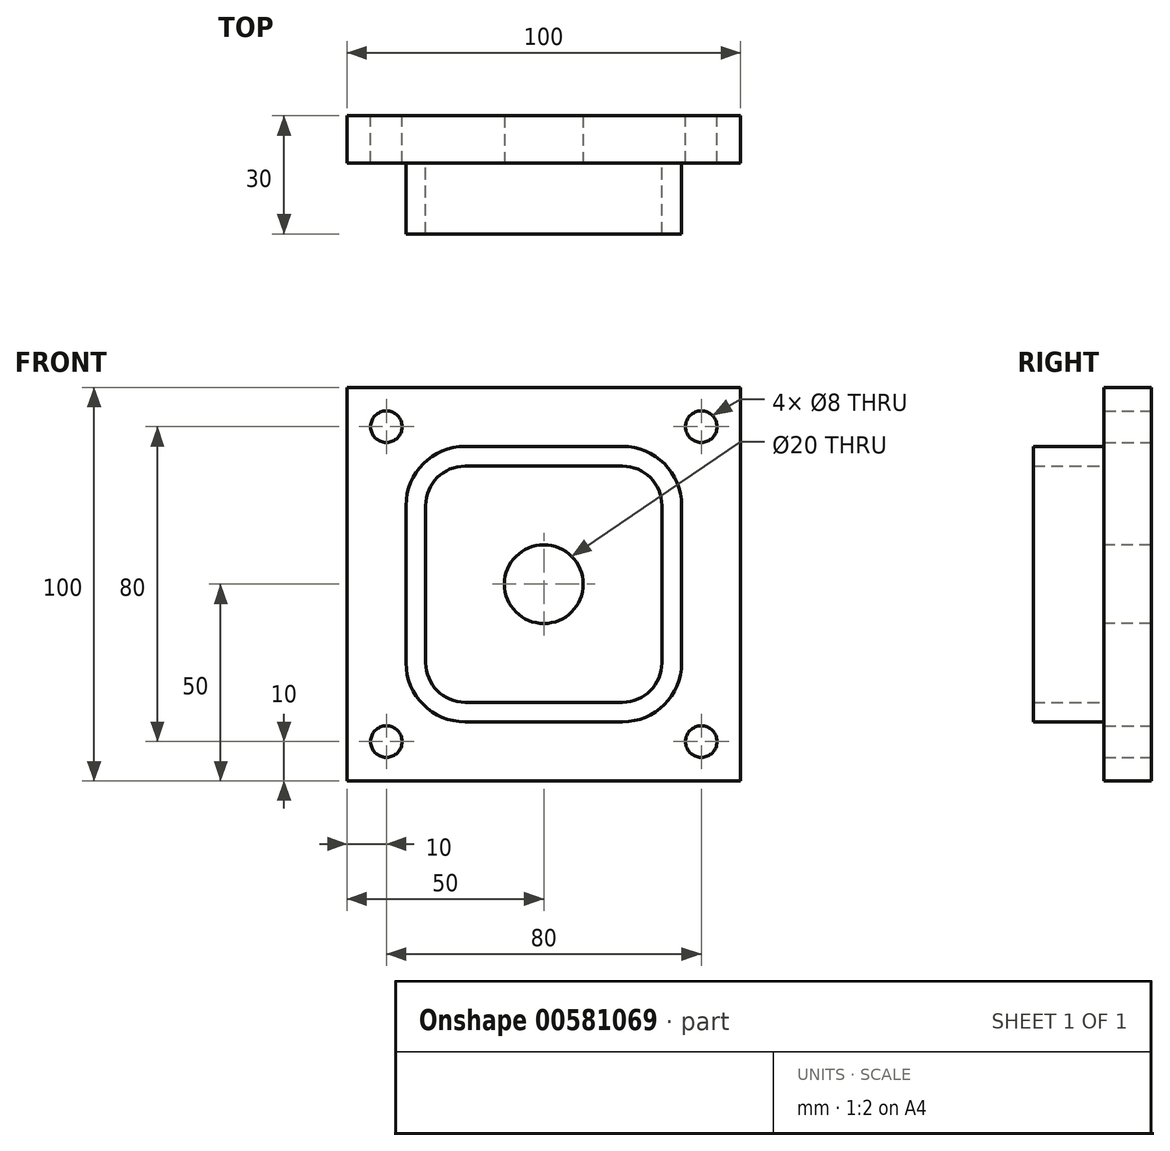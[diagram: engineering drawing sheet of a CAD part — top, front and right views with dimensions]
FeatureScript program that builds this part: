
annotation { "Feature Type Name" : "Feature", "Feature Type Description" : "" }
export const myFeature = defineFeature(function(context is Context, id is Id, definition is map)
    precondition{}
    {
        {
            var Q0;
            Q0=qCreatedBy(makeId("Front.planeOp"),FACE);
            var sketch = newSketch(context, id + "F0", { "sketchPlane" : qUnion([Q0])});
            skLineSegment(sketch, "E0.bottom", {"start": v(50, -50) * mm, "end": v(-50, -50) * mm});
            skLineSegment(sketch, "E0.top", {"start": v(50, 50) * mm, "end": v(-50, 50) * mm});
            skLineSegment(sketch, "E0.left", {"start": v(50, -50) * mm, "end": v(50, 50) * mm});
            skLineSegment(sketch, "E0.right", {"start": v(-50, -50) * mm, "end": v(-50, 50) * mm});
            skPoint(sketch, "E0.middle", {"position": v(0, 0) * mm});
            skCircle(sketch, "E1", {"center": v(-40, 40) * mm, "radius": 4 * mm});
            skCircle(sketch, "E2", {"center": v(-40, -40) * mm, "radius": 4 * mm});
            skCircle(sketch, "E3", {"center": v(40, 40) * mm, "radius": 4 * mm});
            skCircle(sketch, "E4", {"center": v(40, -40) * mm, "radius": 4 * mm});
            skSolve(sketch);
        }
        {
            var Q0;
            Q0=makeQuery(id+"F0.imprint","IMPRINT",FACE,{"disambiguationData":[TD([[makeQuery(id+"F0.imprint","IMPRINT",EDGE,{"derivedFrom":sQuery(id+"F0.wireOp",EDGE,"E0.bottom")}),-1.0]])]});
            extrude(context, id + "F1", {"entities" : qUnion([Q0]), "depth" : 12 * mm, "offsetDistance" : 25 * mm});
        }
        {
            var Q0;
            Q0=makeQuery(id+"F1.opExtrude","CAP_FACE",FACE,{"disambiguationData":[OSD([sQuery(id+"F0.wireOp",EDGE,"E0.bottom"),sQuery(id+"F0.wireOp",EDGE,"E0.top"),sQuery(id+"F0.wireOp",EDGE,"E0.left"),sQuery(id+"F0.wireOp",EDGE,"E0.right"),sQuery(id+"F0.wireOp",EDGE,"E1"),sQuery(id+"F0.wireOp",EDGE,"E2"),sQuery(id+"F0.wireOp",EDGE,"E3"),sQuery(id+"F0.wireOp",EDGE,"E4")])],"isStart":false});
            var sketch = newSketch(context, id + "F2", { "sketchPlane" : qUnion([Q0])});
            skLineSegment(sketch, "E5.bottom", {"start": v(20, -35) * mm, "end": v(-20, -35) * mm});
            skLineSegment(sketch, "E5.top", {"start": v(20, 35) * mm, "end": v(-20, 35) * mm});
            skLineSegment(sketch, "E5.left", {"start": v(35, -20) * mm, "end": v(35, 20) * mm});
            skLineSegment(sketch, "E5.right", {"start": v(-35, -20) * mm, "end": v(-35, 20) * mm});
            skPoint(sketch, "E5.middle", {"position": v(0, 0) * mm});
            skLineSegment(sketch, "E6.bottom", {"start": v(20, -30) * mm, "end": v(-20, -30) * mm});
            skLineSegment(sketch, "E6.top", {"start": v(20, 30) * mm, "end": v(-20, 30) * mm});
            skLineSegment(sketch, "E6.left", {"start": v(30, -20) * mm, "end": v(30, 20) * mm});
            skLineSegment(sketch, "E6.right", {"start": v(-30, -20) * mm, "end": v(-30, 20) * mm});
            skPoint(sketch, "E7.visualSharp", {"position": v(-35, 35) * mm});
            skArc(sketch, "E7.filletArc", {"start": v(-20, 35) * mm, "mid": v(-30.6, 30.6) * mm, "end": v(-35, 20) * mm});
            skPoint(sketch, "E8.visualSharp", {"position": v(-35, -35) * mm});
            skArc(sketch, "E8.filletArc", {"start": v(-35, -20) * mm, "mid": v(-30.6, -30.6) * mm, "end": v(-20, -35) * mm});
            skPoint(sketch, "E9.visualSharp", {"position": v(35, -35) * mm});
            skArc(sketch, "E9.filletArc", {"start": v(20, -35) * mm, "mid": v(30.6, -30.6) * mm, "end": v(35, -20) * mm});
            skPoint(sketch, "E10.visualSharp", {"position": v(35, 35) * mm});
            skArc(sketch, "E10.filletArc", {"start": v(35, 20) * mm, "mid": v(30.6, 30.6) * mm, "end": v(20, 35) * mm});
            skPoint(sketch, "E11.visualSharp", {"position": v(30, 30) * mm});
            skArc(sketch, "E11.filletArc", {"start": v(30, 20) * mm, "mid": v(27.07, 27.07) * mm, "end": v(20, 30) * mm});
            skPoint(sketch, "E12.visualSharp", {"position": v(-30, 30) * mm});
            skArc(sketch, "E12.filletArc", {"start": v(-20, 30) * mm, "mid": v(-27.07, 27.07) * mm, "end": v(-30, 20) * mm});
            skPoint(sketch, "E13.visualSharp", {"position": v(-30, -30) * mm});
            skArc(sketch, "E13.filletArc", {"start": v(-30, -20) * mm, "mid": v(-27.07, -27.07) * mm, "end": v(-20, -30) * mm});
            skPoint(sketch, "E14.visualSharp", {"position": v(30, -30) * mm});
            skArc(sketch, "E14.filletArc", {"start": v(20, -30) * mm, "mid": v(27.07, -27.07) * mm, "end": v(30, -20) * mm});
            skSolve(sketch);
        }
        {
            var Q0;
            Q0=makeQuery(id+"F2.imprint","IMPRINT",FACE,{"disambiguationData":[TD([[makeQuery(id+"F2.imprint","IMPRINT",EDGE,{"derivedFrom":sQuery(id+"F2.wireOp",EDGE,"E5.bottom")}),-1.0]])]});
            extrude(context, id + "F3", {"entities" : qUnion([Q0]), "operationType" : NewBodyOperationType.ADD, "depth" : 18 * mm, "offsetDistance" : 25 * mm});
        }
        {
            var Q0;
            Q0=makeQuery(id+"F3.boolean.opBoolean","SPLIT",FACE,{"disambiguationData":[TD([makeQuery(id+"F3.opExtrude","SWEPT_FACE",FACE,{"disambiguationData":[OSD([sQuery(id+"F2.wireOp",EDGE,"E6.bottom")])]})])],"derivedFrom":makeQuery(id+"F1.opExtrude","CAP_FACE",FACE,{"disambiguationData":[OSD([sQuery(id+"F0.wireOp",EDGE,"E0.bottom"),sQuery(id+"F0.wireOp",EDGE,"E0.top"),sQuery(id+"F0.wireOp",EDGE,"E0.left"),sQuery(id+"F0.wireOp",EDGE,"E0.right"),sQuery(id+"F0.wireOp",EDGE,"E1"),sQuery(id+"F0.wireOp",EDGE,"E2"),sQuery(id+"F0.wireOp",EDGE,"E3"),sQuery(id+"F0.wireOp",EDGE,"E4")])],"isStart":false})});
            var sketch = newSketch(context, id + "F4", { "sketchPlane" : qUnion([Q0])});
            skCircle(sketch, "E15", {"center": v(0, 0) * mm, "radius": 10 * mm});
            skSolve(sketch);
        }
        {
            var Q0;
            Q0=makeQuery(id+"F4.imprint","IMPRINT",FACE,{"disambiguationData":[TD([[makeQuery(id+"F4.imprint","IMPRINT",EDGE,{"derivedFrom":sQuery(id+"F4.wireOp",EDGE,"E15")}),1.0]])]});
            extrude(context, id + "F5", {"entities" : qUnion([Q0]), "operationType" : NewBodyOperationType.REMOVE, "oppositeDirection" : true, "depth" : 12 * mm, "offsetDistance" : 25 * mm});
        }
    });
